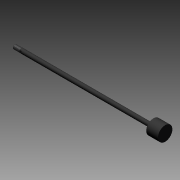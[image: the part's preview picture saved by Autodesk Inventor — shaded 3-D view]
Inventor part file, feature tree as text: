
AUTODESK INVENTOR PART (.ipt)
format: ipt  version: 2014 (Build 180170000, 170)  size: 154,624 bytes
history: native  units: in
note: dims shown in document units (in); Inventor stores cm internally (conversion verified against a paired STEP export)
features: other x98, sketch x3, revolve x2, thread x1, extrude x1
ambient origin geometry x8: Origin, YZ Plane, XZ Plane, XY Plane, X Axis, Y Axis, Z Axis, Center Point
bodies: Solid1 (feature_tree)
feature tree (105):
  revolve  "Revolution1"  Angle=360.0deg
  revolve  "Revolution2"  [1 undecoded]
  thread  "Thread1"  [1 undecoded]
  extrude  "Extrusion1"  [1 undecoded]
  other  "dia1_XY"
  other  "dia1_YZ"
  other  "dia1_ZX"
  other  "dia1_X"
  other  "dia1_Y"
  other  "dia1_Z"
  other  "dia1_Center"
  other  "dia12_XY"
  other  "dia12_YZ"
  other  "dia12_ZX"
  other  "dia12_X"
  other  "dia12_Y"
  other  "dia12_Z"
  other  "dia12_Center"
  other  "dia2_XY"
  other  "dia2_YZ"
  other  "dia2_ZX"
  other  "dia2_X"
  other  "dia2_Y"
  other  "dia2_Z"
  other  "dia2_Center"
  other  "dia22_XY"
  other  "dia22_YZ"
  other  "dia22_ZX"
  other  "dia22_X"
  other  "dia22_Y"
  other  "dia22_Z"
  other  "dia22_Center"
  other  "rl1_XY"
  other  "rl1_YZ"
  other  "rl1_ZX"
  other  "rl1_X"
  other  "rl1_Y"
  other  "rl1_Z"
  other  "rl1_Center"
  other  "rl2_XY"
  other  "rl2_YZ"
  other  "rl2_ZX"
  other  "rl2_X"
  other  "rl2_Y"
  other  "rl2_Z"
  other  "rl2_Center"
  other  "rod_cp_XY"
  other  "rod_cp_YZ"
  other  "rod_cp_ZX"
  other  "rod_cp_X"
  other  "rod_cp_Y"
  other  "rod_cp_Z"
  other  "rod_cp_Center"
  other  "thd1_XY"
  other  "thd1_YZ"
  other  "thd1_ZX"
  other  "thd1_X"
  other  "thd1_Y"
  other  "thd1_Z"
  other  "thd1_Center"
  other  "thd2_XY"
  other  "thd2_YZ"
  other  "thd2_ZX"
  other  "thd2_X"
  other  "thd2_Y"
  other  "thd2_Z"
  other  "thd2_Center"
  other  "to_rod_clevis_XY"
  other  "to_rod_clevis_YZ"
  other  "to_rod_clevis_ZX"
  other  "to_rod_clevis_X"
  other  "to_rod_clevis_Y"
  other  "to_rod_clevis_Z"
  other  "to_rod_clevis_Center"
  other  "wf1_XY"
  other  "wf1_YZ"
  other  "wf1_ZX"
  other  "wf1_X"
  other  "wf1_Y"
  other  "wf1_Z"
  other  "wf1_Center"
  other  "wf2_XY"
  other  "wf2_YZ"
  other  "wf2_ZX"
  other  "wf2_X"
  other  "wf2_Y"
  other  "wf2_Z"
  other  "wf2_Center"
  other  "wfw1_XY"
  other  "wfw1_YZ"
  other  "wfw1_ZX"
  other  "wfw1_X"
  other  "wfw1_Y"
  other  "wfw1_Z"
  other  "wfw1_Center"
  other  "wfw2_XY"
  other  "wfw2_YZ"
  other  "wfw2_ZX"
  other  "wfw2_X"
  other  "wfw2_Y"
  other  "wfw2_Z"
  other  "wfw2_Center"
  sketch  "Sketch_1"  dims[d0=360.0deg d1=360.0deg]
  sketch  "Sketch_3"  dims[d2=0.4752in d3=0.0in d4=0.125in d5=0.0in]
  sketch  "Sketch_10"
note: 3 required parameter values undecoded (feature->parameter linkage not recoverable at this tier; creation-order binding heuristic only, values carry confidence <= 0.55)